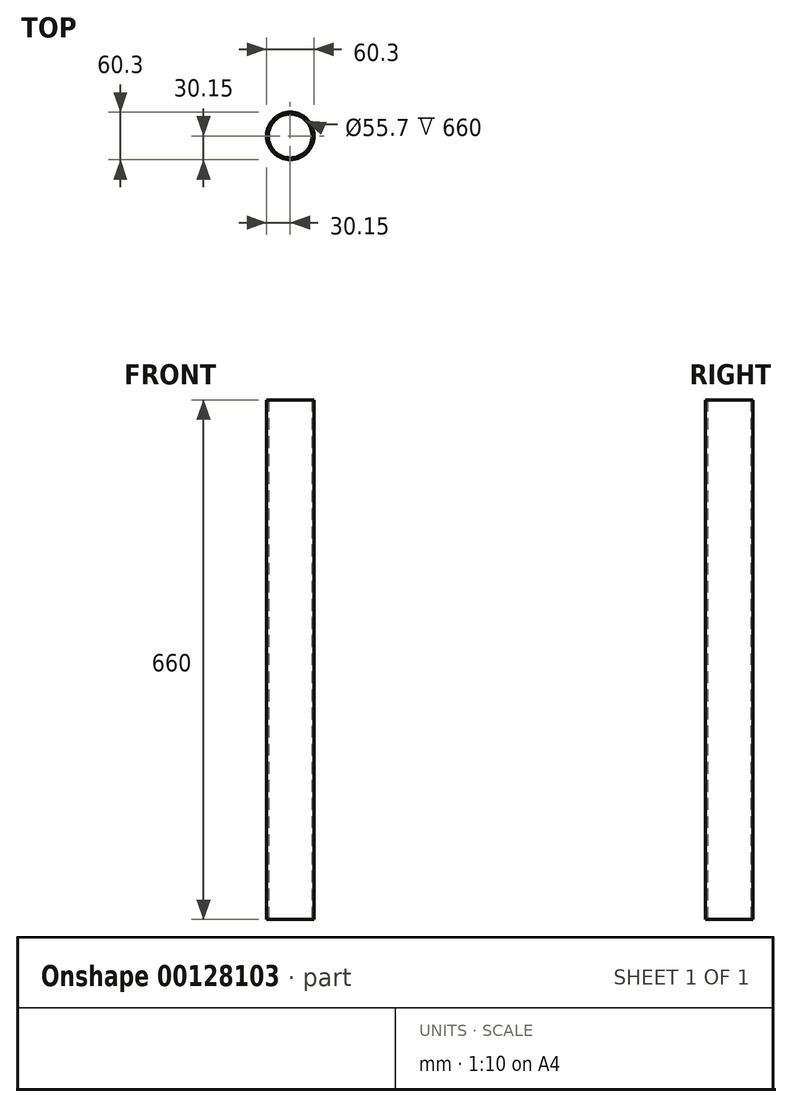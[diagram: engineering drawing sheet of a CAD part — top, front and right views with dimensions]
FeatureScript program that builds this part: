
annotation { "Feature Type Name" : "Feature", "Feature Type Description" : "" }
export const myFeature = defineFeature(function(context is Context, id is Id, definition is map)
    precondition{}
    {
        {
            var Q0;
            Q0=qCreatedBy(makeId("Top.planeOp"),FACE);
            var sketch = newSketch(context, id + "F0", { "sketchPlane" : qUnion([Q0])});
            skCircle(sketch, "E0", {"center": v(0, 0) * mm, "radius": 30.15 * mm});
            skCircle(sketch, "E1", {"center": v(0, 0) * mm, "radius": 27.85 * mm});
            skSolve(sketch);
        }
        {
            var Q0;
            Q0 = qSketchRegion(id + "F0", true);
            extrude(context, id + "F1", {"entities" : qUnion([Q0]), "depth" : 660 * mm});
        }
    });
